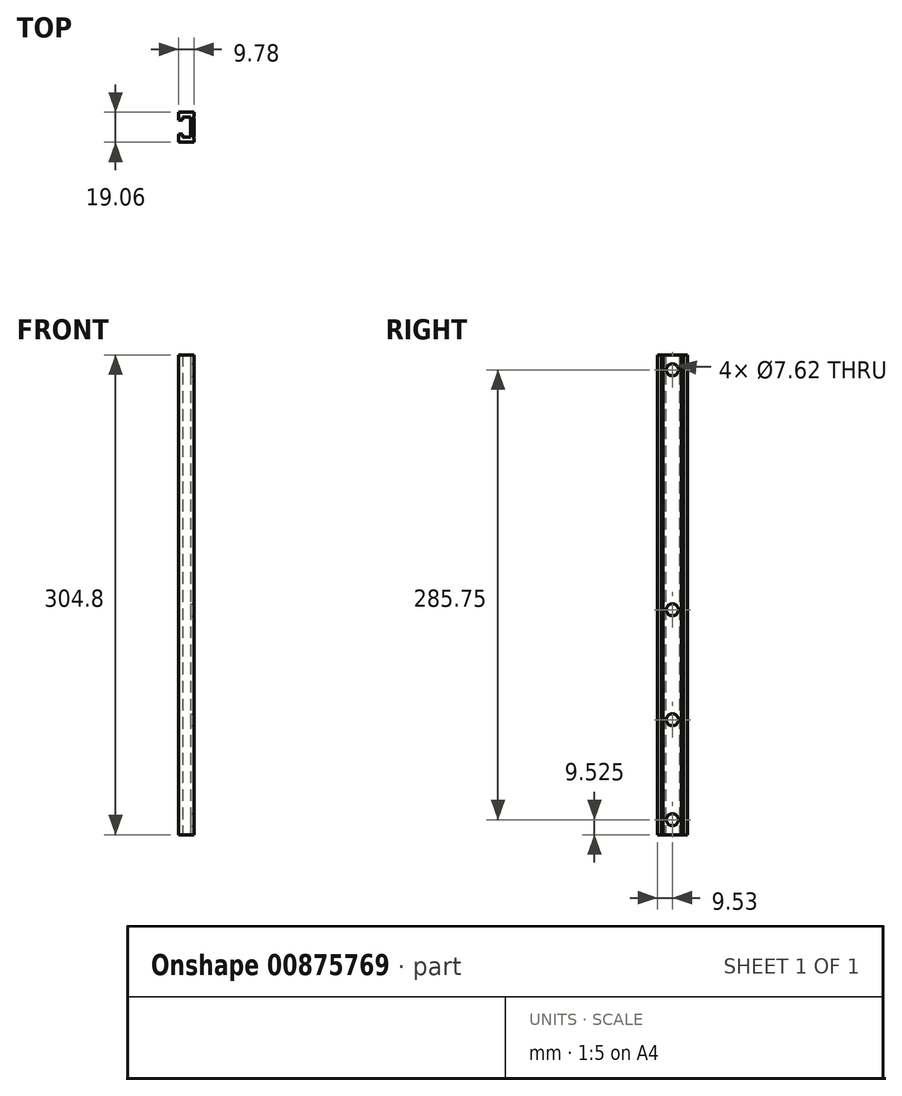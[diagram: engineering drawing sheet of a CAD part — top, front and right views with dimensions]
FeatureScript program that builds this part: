
annotation { "Feature Type Name" : "Feature", "Feature Type Description" : "" }
export const myFeature = defineFeature(function(context is Context, id is Id, definition is map)
    precondition{}
    {
        {
            var Q0;
            Q0=qCreatedBy(makeId("Top.planeOp"),FACE);
            var sketch = newSketch(context, id + "F0", { "sketchPlane" : qUnion([Q0])});
            skLineSegment(sketch, "E0.bottom", {"start": v(4.89, -9.52) * mm, "end": v(-4.89, -9.53) * mm});
            skLineSegment(sketch, "E0.top", {"start": v(4.89, 9.53) * mm, "end": v(-4.89, 9.53) * mm});
            skLineSegment(sketch, "E0.left", {"start": v(4.89, -9.52) * mm, "end": v(4.89, -6.86) * mm});
            skLineSegment(sketch, "E0.right", {"start": v(-4.89, -9.53) * mm, "end": v(-4.89, -4.45) * mm});
            skPoint(sketch, "E0.middle", {"position": v(0, 0) * mm});
            skLineSegment(sketch, "E1.bottom", {"start": v(-2.54, -4.45) * mm, "end": v(-4.89, -4.45) * mm});
            skLineSegment(sketch, "E1.top", {"start": v(-2.54, 4.45) * mm, "end": v(-4.89, 4.45) * mm});
            skPoint(sketch, "E1.middle", {"position": v(-4.89, 0) * mm});
            skLineSegment(sketch, "E2.bottom", {"start": v(2.54, -6.35) * mm, "end": v(-2.54, -6.35) * mm});
            skLineSegment(sketch, "E2.top", {"start": v(2.54, 6.35) * mm, "end": v(-2.54, 6.35) * mm});
            skLineSegment(sketch, "E2.left", {"start": v(2.54, -6.35) * mm, "end": v(2.54, 6.35) * mm});
            skLineSegment(sketch, "E2.right", {"start": v(-2.54, -6.35) * mm, "end": v(-2.54, -4.45) * mm});
            skLineSegment(sketch, "E3.trimOffspring", {"start": v(-4.89, 4.45) * mm, "end": v(-4.89, 9.53) * mm});
            skLineSegment(sketch, "E4.trimOffspring", {"start": v(-2.54, 4.45) * mm, "end": v(-2.54, 6.35) * mm});
            skPoint(sketch, "E5.orphan", {"position": v(-1.71, -4.45) * mm});
            skPoint(sketch, "E6.orphan", {"position": v(-1.71, 4.45) * mm});
            skPoint(sketch, "E7.orphan", {"position": v(-8.06, 4.45) * mm});
            skPoint(sketch, "E8.orphan", {"position": v(-8.06, -4.44) * mm});
            skArc(sketch, "E9", {"start": v(4.89, -5.87) * mm, "mid": v(4.6, -6.37) * mm, "end": v(4.89, -6.86) * mm});
            skArc(sketch, "E10.MirrorCS", {"start": v(4.89, 5.87) * mm, "mid": v(4.6, 6.37) * mm, "end": v(4.89, 6.86) * mm});
            skLineSegment(sketch, "E11.trimOffspring", {"start": v(4.89, 6.86) * mm, "end": v(4.89, 9.53) * mm});
            skLineSegment(sketch, "E12.trimOffspring", {"start": v(4.89, -5.87) * mm, "end": v(4.89, 5.87) * mm});
            skSolve(sketch);
        }
        {
            var Q0;
            Q0 = qSketchRegion(id + "F0", true);
            extrude(context, id + "F1", {"entities" : qUnion([Q0]), "depth" : 304.8 * mm, "offsetDistance" : 25.4 * mm});
        }
        {
            var Q0;
            Q0=makeQuery(id+"F1.opExtrude","SWEPT_FACE",FACE,{"disambiguationData":[OSD([sQuery(id+"F0.wireOp",EDGE,"E12.trimOffspring")])]});
            var sketch = newSketch(context, id + "F2", { "sketchPlane" : qUnion([Q0])});
            skPoint(sketch, "E13", {"position": v(0, 295.28) * mm});
            skPoint(sketch, "E13.positionSnap0", {"position": v(0, 304.8) * mm});
            skPoint(sketch, "E14", {"position": v(0, 142.88) * mm});
            skPoint(sketch, "E15", {"position": v(0, 73.03) * mm});
            skPoint(sketch, "E16", {"position": v(0, 9.53) * mm});
            skSolve(sketch);
        }
        {
            var Q0;
            Q0=sQuery(id+"F2.wireOp",VERTEX,"E13");
            var Q1;
            Q1=sQuery(id+"F2.wireOp",VERTEX,"E14");
            var Q2;
            Q2=sQuery(id+"F2.wireOp",VERTEX,"E15");
            var Q3;
            Q3=sQuery(id+"F2.wireOp",VERTEX,"E16");
            var Q4;
            Q4=makeQuery(id+"F1.opExtrude","SWEPT_BODY",BODY,{"disambiguationData":[OSD([sQuery(id+"F0.wireOp",EDGE,"E0.bottom"),sQuery(id+"F0.wireOp",EDGE,"E0.top"),sQuery(id+"F0.wireOp",EDGE,"E0.left"),sQuery(id+"F0.wireOp",EDGE,"E0.right"),sQuery(id+"F0.wireOp",EDGE,"E1.bottom"),sQuery(id+"F0.wireOp",EDGE,"E1.top"),sQuery(id+"F0.wireOp",EDGE,"E2.bottom"),sQuery(id+"F0.wireOp",EDGE,"E2.top"),sQuery(id+"F0.wireOp",EDGE,"E2.left"),sQuery(id+"F0.wireOp",EDGE,"E2.right"),sQuery(id+"F0.wireOp",EDGE,"E3.trimOffspring"),sQuery(id+"F0.wireOp",EDGE,"E4.trimOffspring"),sQuery(id+"F0.wireOp",EDGE,"E9"),sQuery(id+"F0.wireOp",EDGE,"E10.MirrorCS"),sQuery(id+"F0.wireOp",EDGE,"E11.trimOffspring"),sQuery(id+"F0.wireOp",EDGE,"E12.trimOffspring")])]});
            hole(context, id + "F3", {"style" : HoleStyle.SIMPLE, "endStyle" : HoleEndStyle.BLIND, "holeDiameter" : 7.62 * mm, "majorDiameter" : 6.35 * mm, "holeDepth" : 25.4 * mm, "tappedDepth" : 76.2 * mm, "tapClearance" : 3, "startFromSketch" : true, "locations" : qUnion([Q0, Q1, Q2, Q3]), "scope" : qUnion([Q4])});
        }
    });
